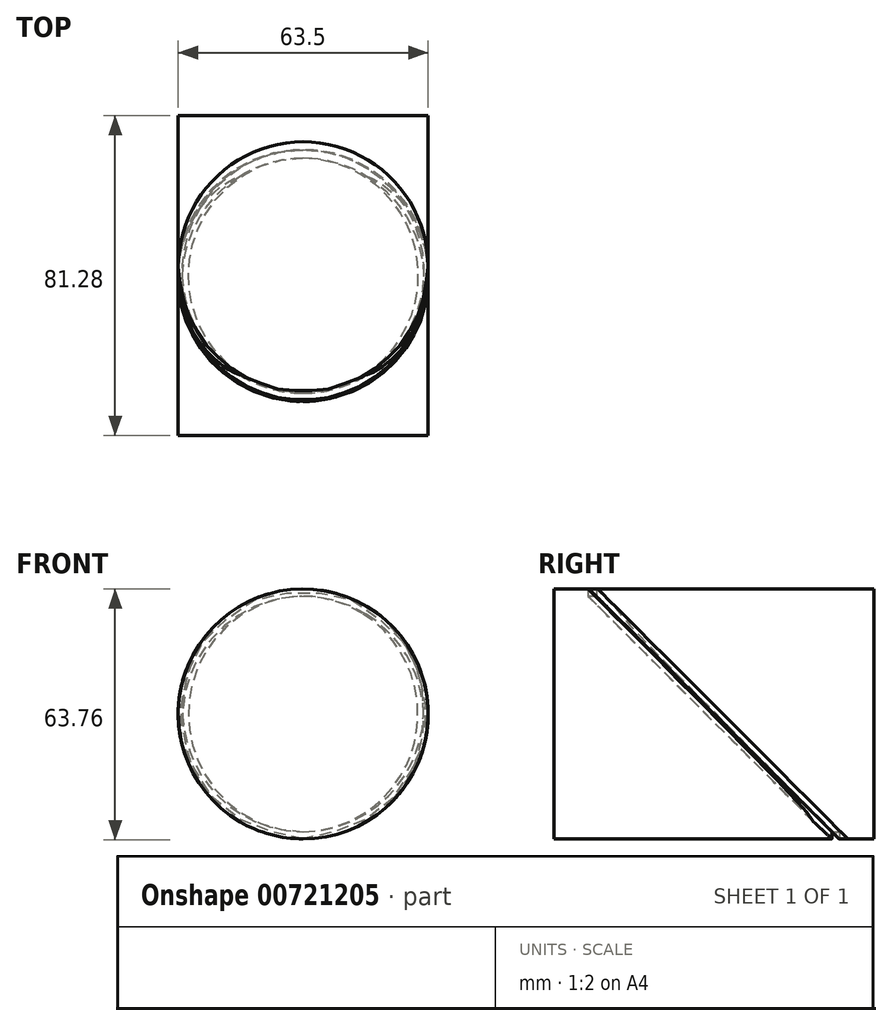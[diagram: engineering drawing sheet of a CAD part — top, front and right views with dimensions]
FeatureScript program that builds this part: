
annotation { "Feature Type Name" : "Feature", "Feature Type Description" : "" }
export const myFeature = defineFeature(function(context is Context, id is Id, definition is map)
    precondition{}
    {
        {
            var Q0;
            Q0=qCreatedBy(makeId("Front.planeOp"),FACE);
            var sketch = newSketch(context, id + "F0", { "sketchPlane" : qUnion([Q0])});
            skCircle(sketch, "E0", {"center": v(0, 0) * mm, "radius": 31.75 * mm});
            skLineSegment(sketch, "E1", {"start": v(-31.75, 0) * mm, "end": v(31.75, 0) * mm, "construction": true});
            skSolve(sketch);
        }
        {
            var Q0;
            Q0 = qSketchRegion(id + "F0", true);
            extrude(context, id + "F1", {"entities" : qUnion([Q0]), "depth" : 81.28 * mm, "offsetDistance" : 25.4 * mm, "symmetric" : true});
        }
        {
            var Q0;
            Q0=sQuery(id+"F0.wireOp",EDGE,"E1");
            cPlane(context, id + "F2", {"entities" : qUnion([Q0]), "cplaneType" : CPlaneType.LINE_ANGLE, "offset" : 25.4 * mm, "angle" : 45 * degree, "width" : 152.4 * mm, "height" : 152.4 * mm});
        }
        {
            var Q0;
            Q0=qCreatedBy(id+"F2.planeOp",FACE);
            var sketch = newSketch(context, id + "F3", { "sketchPlane" : qUnion([Q0])});
            skLineSegment(sketch, "E2.bottom", {"start": v(-31.75, 51.19) * mm, "end": v(31.75, 51.19) * mm});
            skLineSegment(sketch, "E2.top", {"start": v(-31.75, -51.19) * mm, "end": v(31.75, -51.19) * mm});
            skLineSegment(sketch, "E2.left", {"start": v(-31.75, 51.19) * mm, "end": v(-31.75, -51.19) * mm});
            skLineSegment(sketch, "E2.right", {"start": v(31.75, 51.19) * mm, "end": v(31.75, -51.19) * mm});
            skSolve(sketch);
        }
        {
            var Q0;
            Q0=qCreatedBy(makeId("Right.planeOp"),FACE);
            var sketch = newSketch(context, id + "F4", { "sketchPlane" : qUnion([Q0])});
            skLineSegment(sketch, "E3.bottom", {"start": v(-31.75, 31.75) * mm, "end": v(-30.16, 31.75) * mm});
            skLineSegment(sketch, "E3.top", {"start": v(-31.75, 30.16) * mm, "end": v(-30.16, 30.16) * mm});
            skLineSegment(sketch, "E3.left", {"start": v(-31.75, 31.75) * mm, "end": v(-31.75, 30.16) * mm});
            skLineSegment(sketch, "E3.right", {"start": v(-30.16, 31.75) * mm, "end": v(-30.16, 30.16) * mm});
            skLineSegment(sketch, "E4.0", {"start": v(-40.64, -31.75) * mm, "end": v(-40.64, 31.75) * mm, "construction": true});
            skSolve(sketch);
        }
        {
            var Q0;
            Q0=makeQuery(id+"F3.imprint","IMPRINT",FACE,{"disambiguationData":[TD([[makeQuery(id+"F3.imprint","IMPRINT",EDGE,{"derivedFrom":sQuery(id+"F3.wireOp",EDGE,"E2.bottom")}),-1.0]])]});
            extrude(context, id + "F5", {"entities" : qUnion([Q0]), "depth" : 1.59 * mm, "offsetDistance" : 25.4 * mm});
        }
        {
            var Q0;
            Q0=makeQuery(id+"F5.opExtrude","SWEPT_BODY",BODY,{"disambiguationData":[OSD([sQuery(id+"F3.wireOp",EDGE,"E2.bottom"),sQuery(id+"F3.wireOp",EDGE,"E2.top"),sQuery(id+"F3.wireOp",EDGE,"E2.left"),sQuery(id+"F3.wireOp",EDGE,"E2.right")])]});
            var Q1;
            Q1=makeQuery(id+"F1.opExtrude","SWEPT_BODY",BODY,{"disambiguationData":[OSD([sQuery(id+"F0.wireOp",EDGE,"E0")])]});
            booleanBodies(context, id + "F6", {"operationType" : BooleanOperationType.INTERSECTION, "tools" : qUnion([Q0, Q1]), "keepTools" : true});
        }
        {
            var Q0;
            Q0=makeQuery(id+"F5.opExtrude","SWEPT_BODY",BODY,{"disambiguationData":[OSD([sQuery(id+"F3.wireOp",EDGE,"E2.bottom"),sQuery(id+"F3.wireOp",EDGE,"E2.top"),sQuery(id+"F3.wireOp",EDGE,"E2.left"),sQuery(id+"F3.wireOp",EDGE,"E2.right")])]});
            deleteBodies(context, id + "F7", {"entities" : qUnion([Q0])});
        }
        {
            var Q0;
            Q0 = qSketchRegion(id + "F4", true);
            var Q1;
            Q1=makeQuery(id+"F6.opBoolean","INTERSECT",EDGE,{"derivedFrom":[makeQuery(id+"F1.opExtrude","SWEPT_FACE",FACE,{"disambiguationData":[OSD([sQuery(id+"F0.wireOp",EDGE,"E0")])]}),makeQuery(id+"F5.opExtrude","CAP_FACE",FACE,{"disambiguationData":[OSD([sQuery(id+"F3.wireOp",EDGE,"E2.bottom"),sQuery(id+"F3.wireOp",EDGE,"E2.top"),sQuery(id+"F3.wireOp",EDGE,"E2.left"),sQuery(id+"F3.wireOp",EDGE,"E2.right")])],"isStart":true})]});
            sweep(context, id + "F8", {"profiles" : qUnion([Q0]), "path" : qUnion([Q1])});
        }
        {
            var Q0;
            Q0=makeQuery(id+"F8.opSweep","SWEPT_BODY",BODY,{"disambiguationData":[OSD([sQuery(id+"F0.wireOp",EDGE,"E0"),sQuery(id+"F3.wireOp",EDGE,"E2.bottom"),sQuery(id+"F3.wireOp",EDGE,"E2.top"),sQuery(id+"F3.wireOp",EDGE,"E2.left"),sQuery(id+"F3.wireOp",EDGE,"E2.right"),sQuery(id+"F4.wireOp",EDGE,"E3.bottom"),sQuery(id+"F4.wireOp",EDGE,"E3.top"),sQuery(id+"F4.wireOp",EDGE,"E3.left"),sQuery(id+"F4.wireOp",EDGE,"E3.right")])]});
            var Q1;
            Q1=makeQuery(id+"F1.opExtrude","SWEPT_BODY",BODY,{"disambiguationData":[OSD([sQuery(id+"F0.wireOp",EDGE,"E0")])]});
            booleanBodies(context, id + "F9", {"operationType" : BooleanOperationType.SUBTRACTION, "tools" : qUnion([Q0]), "targets" : qUnion([Q1]), "offset" : true, "offsetAll" : true, "offsetDistance" : 0.25 * mm});
        }
    });
